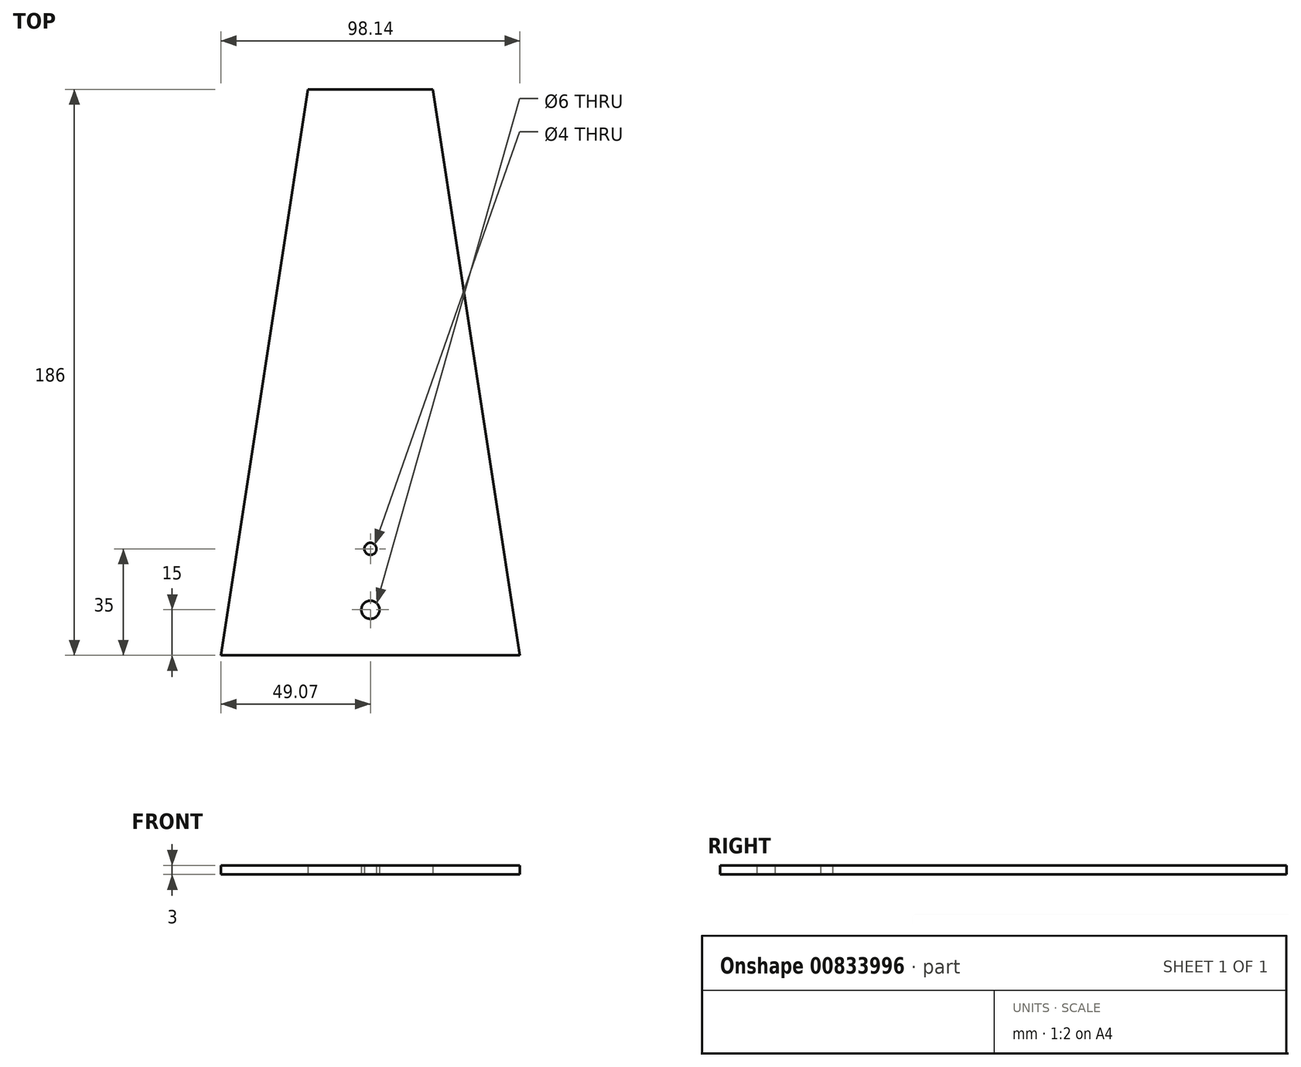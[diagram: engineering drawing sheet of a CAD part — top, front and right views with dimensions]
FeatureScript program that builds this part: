
annotation { "Feature Type Name" : "Feature", "Feature Type Description" : "" }
export const myFeature = defineFeature(function(context is Context, id is Id, definition is map)
    precondition{}
    {
        {
            var Q0;
            Q0=qCreatedBy(makeId("Top.planeOp"),FACE);
            var sketch = newSketch(context, id + "F0", { "sketchPlane" : qUnion([Q0])});
            skLineSegment(sketch, "E0", {"start": v(-46, 0) * mm, "end": v(-20.5, 166) * mm});
            skLineSegment(sketch, "E1", {"start": v(-20.5, 166) * mm, "end": v(20.5, 166) * mm});
            skLineSegment(sketch, "E2", {"start": v(20.5, 166) * mm, "end": v(49.07, -20) * mm});
            skLineSegment(sketch, "E3", {"start": v(46, 0) * mm, "end": v(-46, 0) * mm, "construction": true});
            skLineSegment(sketch, "E4", {"start": v(0, 166) * mm, "end": v(0, 0) * mm, "construction": true});
            skLineSegment(sketch, "E5", {"start": v(-46, 0) * mm, "end": v(-49.07, -20) * mm});
            skLineSegment(sketch, "E6", {"start": v(-49.07, -20) * mm, "end": v(49.07, -20) * mm});
            skCircle(sketch, "E7", {"center": v(0, -5) * mm, "radius": 3 * mm});
            skCircle(sketch, "E8", {"center": v(0, 15) * mm, "radius": 2 * mm});
            skSolve(sketch);
        }
        {
            var Q0;
            Q0=qSketchRegion(id+"F0",true);
            extrude(context, id + "F1", {"entities" : qUnion([Q0]), "depth" : 3 * mm, "offsetDistance" : 25 * mm});
        }
    });
